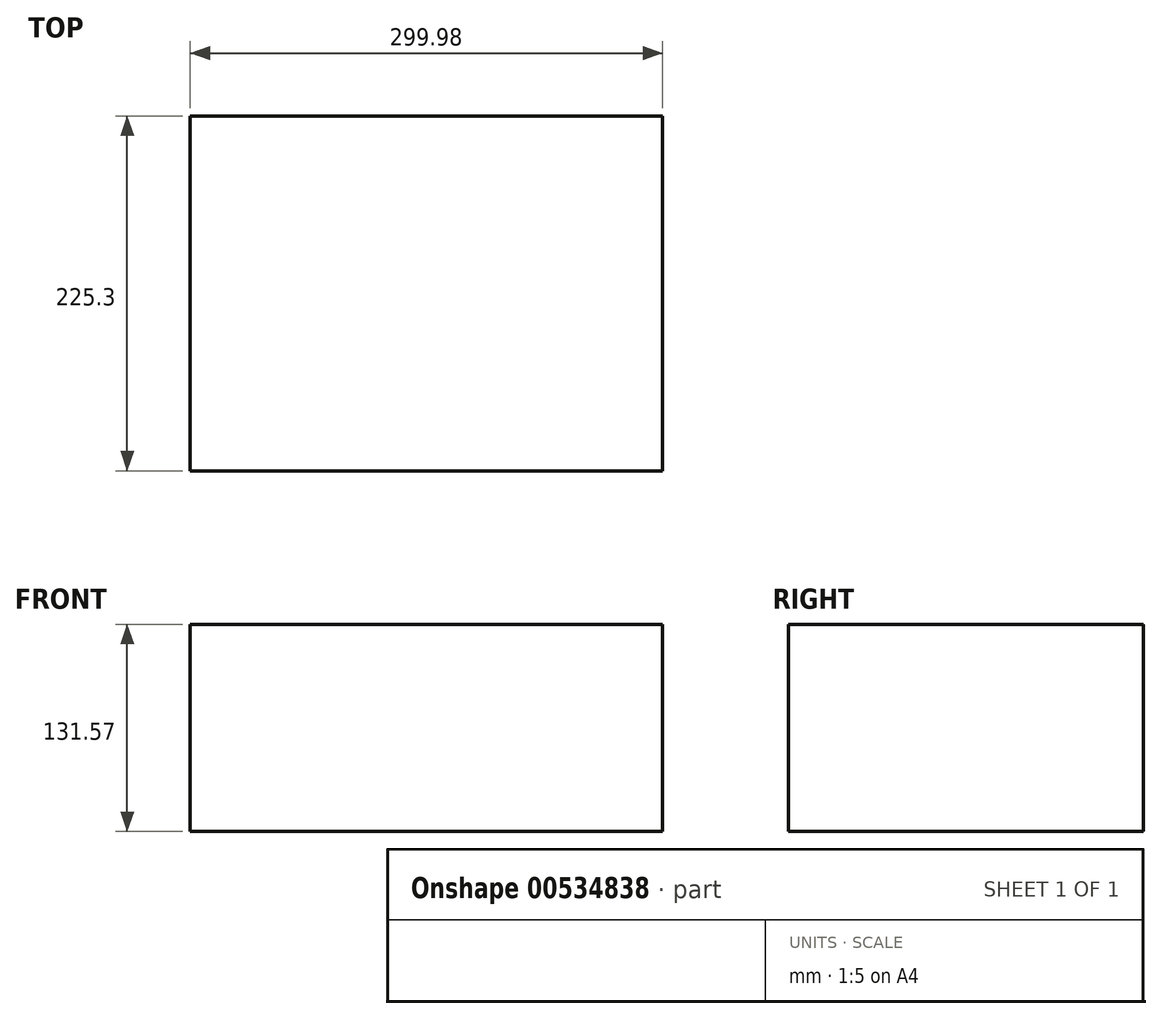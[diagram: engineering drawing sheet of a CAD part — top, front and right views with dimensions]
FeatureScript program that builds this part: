
annotation { "Feature Type Name" : "Feature", "Feature Type Description" : "" }
export const myFeature = defineFeature(function(context is Context, id is Id, definition is map)
    precondition{}
    {
        {
            var Q0;
            Q0=qCreatedBy(makeId("Top.planeOp"),FACE);
            var sketch = newSketch(context, id + "F0", { "sketchPlane" : qUnion([Q0])});
            skLineSegment(sketch, "E0.bottom", {"start": v(149.99, -112.65) * mm, "end": v(-149.99, -112.65) * mm});
            skLineSegment(sketch, "E0.top", {"start": v(149.99, 112.65) * mm, "end": v(-149.99, 112.65) * mm});
            skLineSegment(sketch, "E0.left", {"start": v(149.99, -112.65) * mm, "end": v(149.99, 112.65) * mm});
            skLineSegment(sketch, "E0.right", {"start": v(-149.99, -112.65) * mm, "end": v(-149.99, 112.65) * mm});
            skPoint(sketch, "E0.middle", {"position": v(0, 0) * mm});
            skSolve(sketch);
        }
        {
            var Q0;
            Q0=makeQuery(id+"F0.imprint","IMPRINT",FACE,{"disambiguationData":[TD([[makeQuery(id+"F0.imprint","IMPRINT",EDGE,{"derivedFrom":sQuery(id+"F0.wireOp",EDGE,"E0.bottom")}),-1.0]])]});
            extrude(context, id + "F1", {"entities" : qUnion([Q0]), "depth" : 131.57 * mm, "offsetDistance" : 25.4 * mm});
        }
    });
